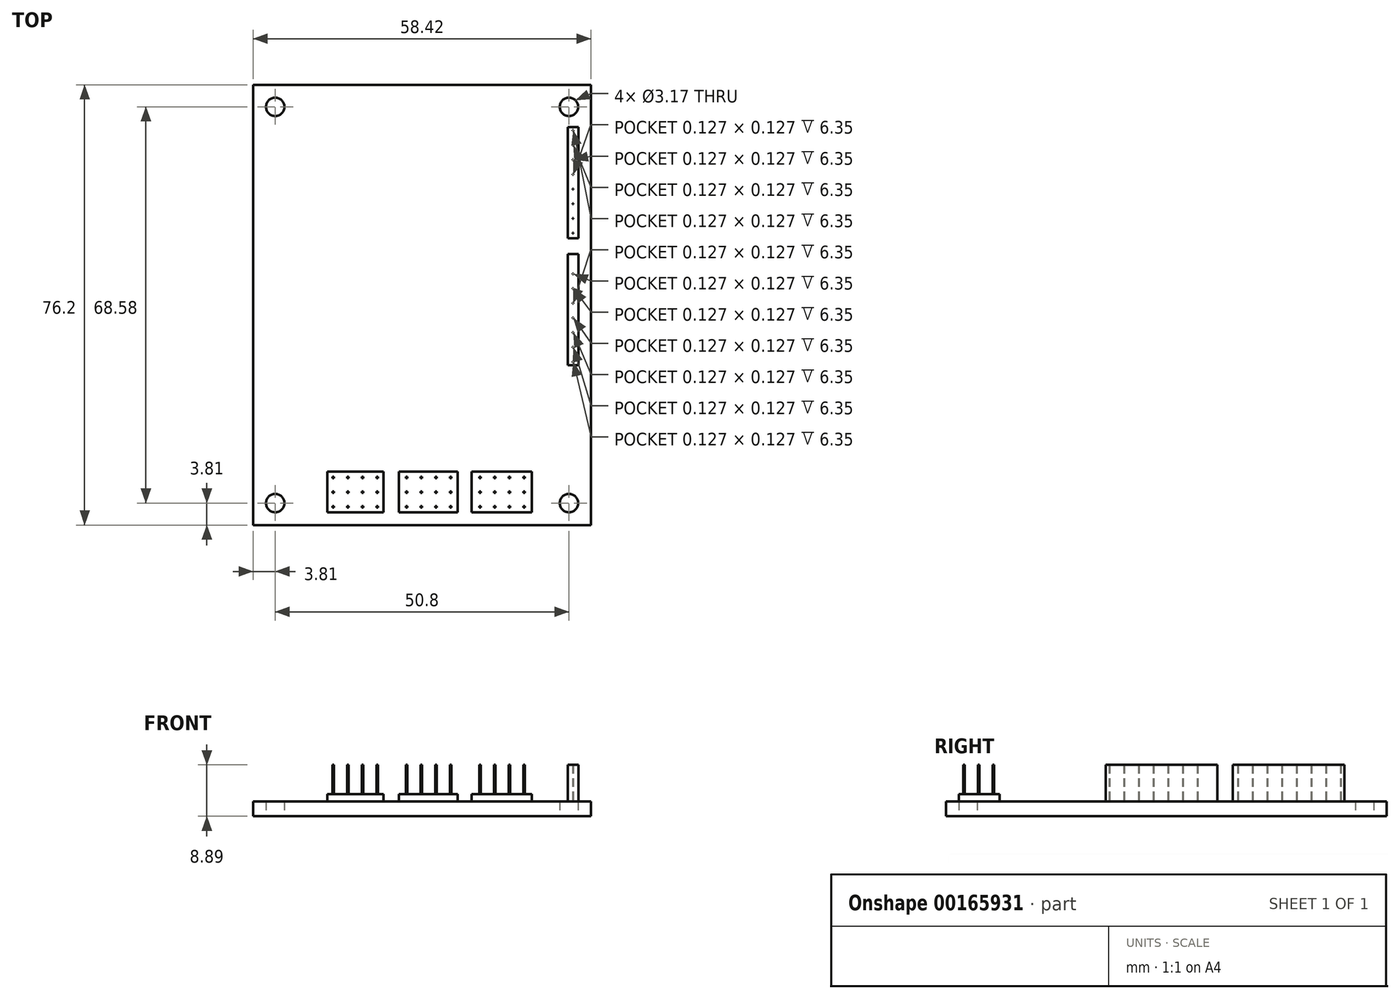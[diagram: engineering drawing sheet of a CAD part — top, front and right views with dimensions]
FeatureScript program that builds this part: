
annotation { "Feature Type Name" : "Feature", "Feature Type Description" : "" }
export const myFeature = defineFeature(function(context is Context, id is Id, definition is map)
    precondition{}
    {
        {
            var Q0;
            Q0=qCreatedBy(makeId("Top.planeOp"),FACE);
            var sketch = newSketch(context, id + "F0", { "sketchPlane" : qUnion([Q0])});
            skLineSegment(sketch, "E0.bottom", {"start": v(-29.21, 38.1) * mm, "end": v(29.21, 38.1) * mm});
            skLineSegment(sketch, "E0.top", {"start": v(-29.21, -38.1) * mm, "end": v(29.21, -38.1) * mm});
            skLineSegment(sketch, "E0.left", {"start": v(-29.21, 38.1) * mm, "end": v(-29.21, -38.1) * mm});
            skLineSegment(sketch, "E0.right", {"start": v(29.21, 38.1) * mm, "end": v(29.2, -38.1) * mm});
            skPoint(sketch, "E1", {"position": v(0, 38.1) * mm});
            skPoint(sketch, "E2", {"position": v(29.21, 0) * mm});
            skCircle(sketch, "E3", {"center": v(-25.4, 34.29) * mm, "radius": 1.59 * mm});
            skLineSegment(sketch, "E4", {"start": v(-25.4, 34.29) * mm, "end": v(-29.2, 34.29) * mm, "construction": true});
            skCircle(sketch, "E5.MirrorC", {"center": v(25.4, 34.29) * mm, "radius": 1.59 * mm});
            skCircle(sketch, "E6.MirrorC", {"center": v(-25.4, -34.29) * mm, "radius": 1.59 * mm});
            skCircle(sketch, "E7.MirrorC", {"center": v(25.4, -34.29) * mm, "radius": 1.59 * mm});
            skSolve(sketch);
        }
        {
            var Q0;
            Q0 = qSketchRegion(id + "F0", true);
            extrude(context, id + "F1", {"entities" : qUnion([Q0]), "depth" : 2.54 * mm});
        }
        {
            var Q0;
            Q0=makeQuery(id+"F1.opExtrude","CAP_FACE",FACE,{"disambiguationData":[OSD([sQuery(id+"F0.wireOp",EDGE,"E0.bottom"),sQuery(id+"F0.wireOp",EDGE,"E0.top"),sQuery(id+"F0.wireOp",EDGE,"E0.left"),sQuery(id+"F0.wireOp",EDGE,"E0.right"),sQuery(id+"F0.wireOp",EDGE,"E3"),sQuery(id+"F0.wireOp",EDGE,"E5.MirrorC"),sQuery(id+"F0.wireOp",EDGE,"E6.MirrorC"),sQuery(id+"F0.wireOp",EDGE,"E7.MirrorC")])],"isStart":false});
            var sketch = newSketch(context, id + "F2", { "sketchPlane" : qUnion([Q0])});
            skLineSegment(sketch, "E8.bottom", {"start": v(26.06, 12.48) * mm, "end": v(26.19, 12.48) * mm});
            skLineSegment(sketch, "E8.top", {"start": v(26.06, 12.35) * mm, "end": v(26.19, 12.35) * mm});
            skLineSegment(sketch, "E8.left", {"start": v(26.06, 12.48) * mm, "end": v(26.06, 12.35) * mm});
            skLineSegment(sketch, "E8.right", {"start": v(26.19, 12.48) * mm, "end": v(26.19, 12.35) * mm});
            skLineSegment(sketch, "E9.1.0.0", {"start": v(26.06, 14.89) * mm, "end": v(26.19, 14.89) * mm});
            skLineSegment(sketch, "E9.1.0.1", {"start": v(26.19, 15.02) * mm, "end": v(26.19, 14.89) * mm});
            skLineSegment(sketch, "E9.1.0.2", {"start": v(26.06, 15.02) * mm, "end": v(26.19, 15.02) * mm});
            skLineSegment(sketch, "E9.1.0.3", {"start": v(26.06, 15.02) * mm, "end": v(26.06, 14.89) * mm});
            skLineSegment(sketch, "E9.2.0.0", {"start": v(26.06, 17.43) * mm, "end": v(26.19, 17.43) * mm});
            skLineSegment(sketch, "E9.2.0.1", {"start": v(26.19, 17.56) * mm, "end": v(26.19, 17.43) * mm});
            skLineSegment(sketch, "E9.2.0.2", {"start": v(26.06, 17.56) * mm, "end": v(26.19, 17.56) * mm});
            skLineSegment(sketch, "E9.2.0.3", {"start": v(26.06, 17.56) * mm, "end": v(26.06, 17.43) * mm});
            skLineSegment(sketch, "E9.direction1", {"start": v(26.06, 12.35) * mm, "end": v(26.06, 14.89) * mm, "construction": true});
            skLineSegment(sketch, "E10.0.3.0", {"start": v(26.06, 19.97) * mm, "end": v(26.19, 19.97) * mm});
            skLineSegment(sketch, "E10.3.3.0", {"start": v(26.19, 20.1) * mm, "end": v(26.19, 19.97) * mm});
            skLineSegment(sketch, "E10.6.3.0", {"start": v(26.06, 20.1) * mm, "end": v(26.19, 20.1) * mm});
            skLineSegment(sketch, "E10.9.3.0", {"start": v(26.06, 20.1) * mm, "end": v(26.06, 19.97) * mm});
            skLineSegment(sketch, "E10.0.4.0", {"start": v(26.06, 22.5) * mm, "end": v(26.19, 22.5) * mm});
            skLineSegment(sketch, "E10.3.4.0", {"start": v(26.19, 22.64) * mm, "end": v(26.19, 22.5) * mm});
            skLineSegment(sketch, "E10.6.4.0", {"start": v(26.06, 22.64) * mm, "end": v(26.19, 22.64) * mm});
            skLineSegment(sketch, "E10.9.4.0", {"start": v(26.06, 22.64) * mm, "end": v(26.06, 22.5) * mm});
            skLineSegment(sketch, "E10.0.5.0", {"start": v(26.06, 25.05) * mm, "end": v(26.19, 25.05) * mm});
            skLineSegment(sketch, "E10.3.5.0", {"start": v(26.19, 25.18) * mm, "end": v(26.19, 25.05) * mm});
            skLineSegment(sketch, "E10.6.5.0", {"start": v(26.06, 25.18) * mm, "end": v(26.19, 25.18) * mm});
            skLineSegment(sketch, "E10.9.5.0", {"start": v(26.06, 25.18) * mm, "end": v(26.06, 25.05) * mm});
            skLineSegment(sketch, "E10.0.6.0", {"start": v(26.06, 27.59) * mm, "end": v(26.19, 27.59) * mm});
            skLineSegment(sketch, "E10.3.6.0", {"start": v(26.19, 27.72) * mm, "end": v(26.19, 27.59) * mm});
            skLineSegment(sketch, "E10.6.6.0", {"start": v(26.06, 27.72) * mm, "end": v(26.19, 27.72) * mm});
            skLineSegment(sketch, "E10.9.6.0", {"start": v(26.06, 27.72) * mm, "end": v(26.06, 27.59) * mm});
            skLineSegment(sketch, "E10.0.7.0", {"start": v(26.06, 30.13) * mm, "end": v(26.19, 30.13) * mm});
            skLineSegment(sketch, "E10.3.7.0", {"start": v(26.19, 30.26) * mm, "end": v(26.19, 30.13) * mm});
            skLineSegment(sketch, "E10.6.7.0", {"start": v(26.06, 30.26) * mm, "end": v(26.19, 30.26) * mm});
            skLineSegment(sketch, "E10.9.7.0", {"start": v(26.06, 30.26) * mm, "end": v(26.06, 30.13) * mm});
            skLineSegment(sketch, "E11.bottom", {"start": v(25.22, 30.8) * mm, "end": v(27.07, 30.8) * mm});
            skLineSegment(sketch, "E11.top", {"start": v(25.22, 11.52) * mm, "end": v(27.07, 11.52) * mm});
            skLineSegment(sketch, "E11.left", {"start": v(25.22, 30.8) * mm, "end": v(25.22, 11.52) * mm});
            skLineSegment(sketch, "E11.right", {"start": v(27.07, 30.8) * mm, "end": v(27.07, 11.52) * mm});
            skLineSegment(sketch, "E12", {"start": v(29.21, 10.17) * mm, "end": v(23.82, 10.17) * mm, "construction": true});
            skLineSegment(sketch, "E13.MirrorCS", {"start": v(25.22, -10.45) * mm, "end": v(25.22, 8.82) * mm});
            skLineSegment(sketch, "E14.MirrorCS", {"start": v(26.06, 8) * mm, "end": v(26.19, 8) * mm});
            skLineSegment(sketch, "E15.MirrorCS", {"start": v(26.06, 8) * mm, "end": v(26.06, 5.46) * mm, "construction": true});
            skLineSegment(sketch, "E16.MirrorCS", {"start": v(26.06, 7.87) * mm, "end": v(26.19, 7.87) * mm});
            skLineSegment(sketch, "E17.MirrorCS", {"start": v(26.19, 7.87) * mm, "end": v(26.19, 8) * mm});
            skLineSegment(sketch, "E18.MirrorCS", {"start": v(26.19, 5.33) * mm, "end": v(26.19, 5.46) * mm});
            skLineSegment(sketch, "E19.MirrorCS", {"start": v(26.06, 5.33) * mm, "end": v(26.19, 5.33) * mm});
            skLineSegment(sketch, "E20.MirrorCS", {"start": v(26.06, 5.33) * mm, "end": v(26.06, 5.46) * mm});
            skLineSegment(sketch, "E21.MirrorCS", {"start": v(26.06, 5.46) * mm, "end": v(26.19, 5.46) * mm});
            skLineSegment(sketch, "E22.MirrorCS", {"start": v(26.19, 2.79) * mm, "end": v(26.19, 2.92) * mm});
            skLineSegment(sketch, "E23.MirrorCS", {"start": v(26.06, 2.79) * mm, "end": v(26.19, 2.79) * mm});
            skLineSegment(sketch, "E24.MirrorCS", {"start": v(26.06, 2.79) * mm, "end": v(26.06, 2.92) * mm});
            skLineSegment(sketch, "E25.MirrorCS", {"start": v(26.06, 2.92) * mm, "end": v(26.19, 2.92) * mm});
            skLineSegment(sketch, "E26.MirrorCS", {"start": v(26.06, 0.38) * mm, "end": v(26.19, 0.38) * mm});
            skLineSegment(sketch, "E27.MirrorCS", {"start": v(26.19, 0.25) * mm, "end": v(26.19, 0.38) * mm});
            skLineSegment(sketch, "E28.MirrorCS", {"start": v(26.06, 0.25) * mm, "end": v(26.19, 0.25) * mm});
            skLineSegment(sketch, "E29.MirrorCS", {"start": v(26.06, 0.25) * mm, "end": v(26.06, 0.38) * mm});
            skLineSegment(sketch, "E30.MirrorCS", {"start": v(26.19, -2.3) * mm, "end": v(26.19, -2.16) * mm});
            skLineSegment(sketch, "E31.MirrorCS", {"start": v(26.06, -2.3) * mm, "end": v(26.19, -2.3) * mm});
            skLineSegment(sketch, "E32.MirrorCS", {"start": v(26.06, -2.3) * mm, "end": v(26.06, -2.16) * mm});
            skLineSegment(sketch, "E33.MirrorCS", {"start": v(26.06, -2.16) * mm, "end": v(26.19, -2.16) * mm});
            skLineSegment(sketch, "E34.MirrorCS", {"start": v(26.06, -7.37) * mm, "end": v(26.19, -7.37) * mm});
            skLineSegment(sketch, "E35.MirrorCS", {"start": v(26.06, -4.83) * mm, "end": v(26.19, -4.83) * mm});
            skLineSegment(sketch, "E36.MirrorCS", {"start": v(26.19, -7.37) * mm, "end": v(26.19, -7.24) * mm});
            skLineSegment(sketch, "E37.MirrorCS", {"start": v(26.19, -4.83) * mm, "end": v(26.19, -4.7) * mm});
            skLineSegment(sketch, "E38.MirrorCS", {"start": v(26.06, -4.83) * mm, "end": v(26.06, -4.7) * mm});
            skLineSegment(sketch, "E39.MirrorCS", {"start": v(26.06, -7.24) * mm, "end": v(26.19, -7.24) * mm});
            skLineSegment(sketch, "E40.MirrorCS", {"start": v(26.06, -4.7) * mm, "end": v(26.19, -4.7) * mm});
            skLineSegment(sketch, "E41.MirrorCS", {"start": v(26.06, -7.37) * mm, "end": v(26.06, -7.24) * mm});
            skLineSegment(sketch, "E42.MirrorCS", {"start": v(26.06, -9.78) * mm, "end": v(26.19, -9.78) * mm});
            skLineSegment(sketch, "E43.MirrorCS", {"start": v(26.06, -9.91) * mm, "end": v(26.19, -9.91) * mm});
            skLineSegment(sketch, "E44.MirrorCS", {"start": v(26.06, -9.91) * mm, "end": v(26.06, -9.78) * mm});
            skLineSegment(sketch, "E45.MirrorCS", {"start": v(26.19, -9.91) * mm, "end": v(26.19, -9.78) * mm});
            skLineSegment(sketch, "E46.MirrorCS", {"start": v(25.22, 8.82) * mm, "end": v(27.07, 8.82) * mm});
            skLineSegment(sketch, "E47.MirrorCS", {"start": v(27.07, -10.45) * mm, "end": v(27.07, 8.82) * mm});
            skLineSegment(sketch, "E48.MirrorCS", {"start": v(25.22, -10.45) * mm, "end": v(27.07, -10.45) * mm});
            skSolve(sketch);
        }
        {
            var Q0;
            Q0 = qSketchRegion(id + "F2", true);
            extrude(context, id + "F3", {"entities" : qUnion([Q0]), "operationType" : NewBodyOperationType.ADD, "depth" : 6.35 * mm});
        }
        {
            var Q0;
            {var subQ0=sQuery(id+"F0.wireOp",EDGE,"E0.left");var subQ1=sQuery(id+"F0.wireOp",EDGE,"E7.MirrorC");var subQ2=sQuery(id+"F0.wireOp",EDGE,"E6.MirrorC");var subQ3=sQuery(id+"F0.wireOp",EDGE,"E5.MirrorC");var subQ4=sQuery(id+"F0.wireOp",EDGE,"E3");var subQ5=sQuery(id+"F0.wireOp",EDGE,"E0.right");var subQ6=sQuery(id+"F0.wireOp",EDGE,"E0.bottom");var subQ7=sQuery(id+"F0.wireOp",EDGE,"E0.top");Q0=makeQuery(id+"F3.boolean.opBoolean","SPLIT",FACE,{"disambiguationData":[TD([makeQuery(id+"F1.opExtrude","SWEPT_FACE",FACE,{"disambiguationData":[OSD([subQ6])]})])],"derivedFrom":makeQuery(id+"F1.opExtrude","CAP_FACE",FACE,{"disambiguationData":[OSD([subQ6,subQ7,subQ0,subQ5,subQ4,subQ3,subQ2,subQ1])],"isStart":false})});}
            var sketch = newSketch(context, id + "F4", { "sketchPlane" : qUnion([Q0])});
            skLineSegment(sketch, "E49.bottom", {"start": v(-15.5, -34.83) * mm, "end": v(-15.24, -34.83) * mm});
            skLineSegment(sketch, "E49.top", {"start": v(-15.5, -35.09) * mm, "end": v(-15.24, -35.09) * mm});
            skLineSegment(sketch, "E49.left", {"start": v(-15.5, -34.83) * mm, "end": v(-15.5, -35.09) * mm});
            skLineSegment(sketch, "E49.right", {"start": v(-15.24, -34.83) * mm, "end": v(-15.24, -35.09) * mm});
            skLineSegment(sketch, "E50.1.0.0", {"start": v(-12.7, -34.83) * mm, "end": v(-12.7, -35.09) * mm});
            skLineSegment(sketch, "E50.1.0.1", {"start": v(-12.95, -34.83) * mm, "end": v(-12.95, -35.09) * mm});
            skLineSegment(sketch, "E50.1.0.2", {"start": v(-12.95, -34.83) * mm, "end": v(-12.7, -34.83) * mm});
            skLineSegment(sketch, "E50.1.0.3", {"start": v(-12.95, -35.09) * mm, "end": v(-12.7, -35.09) * mm});
            skLineSegment(sketch, "E50.2.0.0", {"start": v(-10.16, -34.83) * mm, "end": v(-10.16, -35.09) * mm});
            skLineSegment(sketch, "E50.2.0.1", {"start": v(-10.41, -34.83) * mm, "end": v(-10.41, -35.09) * mm});
            skLineSegment(sketch, "E50.2.0.2", {"start": v(-10.41, -34.83) * mm, "end": v(-10.16, -34.83) * mm});
            skLineSegment(sketch, "E50.2.0.3", {"start": v(-10.41, -35.09) * mm, "end": v(-10.16, -35.09) * mm});
            skLineSegment(sketch, "E50.3.0.0", {"start": v(-7.62, -34.83) * mm, "end": v(-7.62, -35.09) * mm});
            skLineSegment(sketch, "E50.3.0.1", {"start": v(-7.87, -34.83) * mm, "end": v(-7.87, -35.09) * mm});
            skLineSegment(sketch, "E50.3.0.2", {"start": v(-7.87, -34.83) * mm, "end": v(-7.62, -34.83) * mm});
            skLineSegment(sketch, "E50.3.0.3", {"start": v(-7.87, -35.09) * mm, "end": v(-7.62, -35.09) * mm});
            skLineSegment(sketch, "E50.direction1", {"start": v(-15.5, -35.09) * mm, "end": v(-12.95, -35.09) * mm, "construction": true});
            skLineSegment(sketch, "E51.1.0.0", {"start": v(-15.5, -32.55) * mm, "end": v(-12.95, -32.55) * mm, "construction": true});
            skLineSegment(sketch, "E51.1.0.1", {"start": v(-7.87, -32.3) * mm, "end": v(-7.62, -32.3) * mm});
            skLineSegment(sketch, "E51.1.0.2", {"start": v(-7.87, -32.3) * mm, "end": v(-7.87, -32.55) * mm});
            skLineSegment(sketch, "E51.1.0.3", {"start": v(-7.87, -32.55) * mm, "end": v(-7.62, -32.55) * mm});
            skLineSegment(sketch, "E51.1.0.4", {"start": v(-15.5, -32.3) * mm, "end": v(-15.24, -32.3) * mm});
            skLineSegment(sketch, "E51.1.0.5", {"start": v(-15.5, -32.3) * mm, "end": v(-15.5, -32.55) * mm});
            skLineSegment(sketch, "E51.1.0.6", {"start": v(-15.24, -32.3) * mm, "end": v(-15.24, -32.55) * mm});
            skLineSegment(sketch, "E51.1.0.7", {"start": v(-12.7, -32.3) * mm, "end": v(-12.7, -32.55) * mm});
            skLineSegment(sketch, "E51.1.0.8", {"start": v(-12.95, -32.3) * mm, "end": v(-12.7, -32.3) * mm});
            skLineSegment(sketch, "E51.1.0.9", {"start": v(-10.16, -32.3) * mm, "end": v(-10.16, -32.55) * mm});
            skLineSegment(sketch, "E51.1.0.10", {"start": v(-10.41, -32.3) * mm, "end": v(-10.41, -32.55) * mm});
            skLineSegment(sketch, "E51.1.0.11", {"start": v(-10.41, -32.3) * mm, "end": v(-10.16, -32.3) * mm});
            skLineSegment(sketch, "E51.1.0.12", {"start": v(-10.41, -32.55) * mm, "end": v(-10.16, -32.55) * mm});
            skLineSegment(sketch, "E51.1.0.13", {"start": v(-7.62, -32.3) * mm, "end": v(-7.62, -32.55) * mm});
            skLineSegment(sketch, "E51.1.0.14", {"start": v(-15.5, -32.55) * mm, "end": v(-15.24, -32.55) * mm});
            skLineSegment(sketch, "E51.1.0.15", {"start": v(-12.95, -32.3) * mm, "end": v(-12.95, -32.55) * mm});
            skLineSegment(sketch, "E51.1.0.16", {"start": v(-12.95, -32.55) * mm, "end": v(-12.7, -32.55) * mm});
            skLineSegment(sketch, "E51.2.0.0", {"start": v(-15.5, -30) * mm, "end": v(-12.95, -30) * mm, "construction": true});
            skLineSegment(sketch, "E51.2.0.1", {"start": v(-7.87, -29.75) * mm, "end": v(-7.62, -29.75) * mm});
            skLineSegment(sketch, "E51.2.0.2", {"start": v(-7.87, -29.75) * mm, "end": v(-7.87, -30) * mm});
            skLineSegment(sketch, "E51.2.0.3", {"start": v(-7.87, -30) * mm, "end": v(-7.62, -30) * mm});
            skLineSegment(sketch, "E51.2.0.4", {"start": v(-15.5, -29.75) * mm, "end": v(-15.24, -29.75) * mm});
            skLineSegment(sketch, "E51.2.0.5", {"start": v(-15.5, -29.75) * mm, "end": v(-15.5, -30) * mm});
            skLineSegment(sketch, "E51.2.0.6", {"start": v(-15.24, -29.75) * mm, "end": v(-15.24, -30) * mm});
            skLineSegment(sketch, "E51.2.0.7", {"start": v(-12.7, -29.75) * mm, "end": v(-12.7, -30) * mm});
            skLineSegment(sketch, "E51.2.0.8", {"start": v(-12.95, -29.75) * mm, "end": v(-12.7, -29.75) * mm});
            skLineSegment(sketch, "E51.2.0.9", {"start": v(-10.16, -29.75) * mm, "end": v(-10.16, -30) * mm});
            skLineSegment(sketch, "E51.2.0.10", {"start": v(-10.41, -29.75) * mm, "end": v(-10.41, -30) * mm});
            skLineSegment(sketch, "E51.2.0.11", {"start": v(-10.41, -29.75) * mm, "end": v(-10.16, -29.75) * mm});
            skLineSegment(sketch, "E51.2.0.12", {"start": v(-10.41, -30) * mm, "end": v(-10.16, -30) * mm});
            skLineSegment(sketch, "E51.2.0.13", {"start": v(-7.62, -29.75) * mm, "end": v(-7.62, -30) * mm});
            skLineSegment(sketch, "E51.2.0.14", {"start": v(-15.5, -30) * mm, "end": v(-15.24, -30) * mm});
            skLineSegment(sketch, "E51.2.0.15", {"start": v(-12.95, -29.75) * mm, "end": v(-12.95, -30) * mm});
            skLineSegment(sketch, "E51.2.0.16", {"start": v(-12.95, -30) * mm, "end": v(-12.7, -30) * mm});
            skLineSegment(sketch, "E51.direction1", {"start": v(-15.5, -35.09) * mm, "end": v(-15.5, -32.55) * mm, "construction": true});
            skLineSegment(sketch, "E52.1.0.0", {"start": v(-2.8, -35.09) * mm, "end": v(-2.8, -32.55) * mm, "construction": true});
            skLineSegment(sketch, "E52.1.0.1", {"start": v(-2.8, -30) * mm, "end": v(-0.25, -30) * mm, "construction": true});
            skLineSegment(sketch, "E52.1.0.2", {"start": v(-2.8, -35.09) * mm, "end": v(-0.25, -35.09) * mm, "construction": true});
            skLineSegment(sketch, "E52.1.0.3", {"start": v(-2.8, -32.55) * mm, "end": v(-0.25, -32.55) * mm, "construction": true});
            skLineSegment(sketch, "E52.1.0.4", {"start": v(2.29, -32.3) * mm, "end": v(2.29, -32.55) * mm});
            skLineSegment(sketch, "E52.1.0.5", {"start": v(4.83, -32.3) * mm, "end": v(4.83, -32.55) * mm});
            skLineSegment(sketch, "E52.1.0.6", {"start": v(4.83, -29.75) * mm, "end": v(5.08, -29.75) * mm});
            skLineSegment(sketch, "E52.1.0.7", {"start": v(4.83, -32.3) * mm, "end": v(5.08, -32.3) * mm});
            skLineSegment(sketch, "E52.1.0.8", {"start": v(2.29, -32.55) * mm, "end": v(2.54, -32.55) * mm});
            skLineSegment(sketch, "E52.1.0.9", {"start": v(4.83, -29.75) * mm, "end": v(4.83, -30) * mm});
            skLineSegment(sketch, "E52.1.0.10", {"start": v(4.83, -32.55) * mm, "end": v(5.08, -32.55) * mm});
            skLineSegment(sketch, "E52.1.0.11", {"start": v(2.29, -29.75) * mm, "end": v(2.54, -29.75) * mm});
            skLineSegment(sketch, "E52.1.0.12", {"start": v(4.83, -34.83) * mm, "end": v(5.08, -34.83) * mm});
            skLineSegment(sketch, "E52.1.0.13", {"start": v(4.83, -35.09) * mm, "end": v(5.08, -35.09) * mm});
            skLineSegment(sketch, "E52.1.0.14", {"start": v(2.29, -34.83) * mm, "end": v(2.29, -35.09) * mm});
            skLineSegment(sketch, "E52.1.0.15", {"start": v(2.29, -34.83) * mm, "end": v(2.54, -34.83) * mm});
            skLineSegment(sketch, "E52.1.0.16", {"start": v(2.29, -29.75) * mm, "end": v(2.29, -30) * mm});
            skLineSegment(sketch, "E52.1.0.17", {"start": v(2.29, -32.3) * mm, "end": v(2.54, -32.3) * mm});
            skLineSegment(sketch, "E52.1.0.18", {"start": v(2.29, -35.09) * mm, "end": v(2.54, -35.09) * mm});
            skLineSegment(sketch, "E52.1.0.19", {"start": v(5.08, -34.83) * mm, "end": v(5.08, -35.09) * mm});
            skLineSegment(sketch, "E52.1.0.20", {"start": v(4.83, -30) * mm, "end": v(5.08, -30) * mm});
            skLineSegment(sketch, "E52.1.0.21", {"start": v(5.08, -32.3) * mm, "end": v(5.08, -32.55) * mm});
            skLineSegment(sketch, "E52.1.0.22", {"start": v(2.29, -30) * mm, "end": v(2.54, -30) * mm});
            skLineSegment(sketch, "E52.1.0.23", {"start": v(-2.8, -30) * mm, "end": v(-2.54, -30) * mm});
            skLineSegment(sketch, "E52.1.0.24", {"start": v(2.54, -29.75) * mm, "end": v(2.54, -30) * mm});
            skLineSegment(sketch, "E52.1.0.25", {"start": v(2.54, -32.3) * mm, "end": v(2.54, -32.55) * mm});
            skLineSegment(sketch, "E52.1.0.26", {"start": v(-0.25, -29.75) * mm, "end": v(0, -29.75) * mm});
            skLineSegment(sketch, "E52.1.0.27", {"start": v(-0.25, -30) * mm, "end": v(0, -30) * mm});
            skLineSegment(sketch, "E52.1.0.28", {"start": v(5.08, -29.75) * mm, "end": v(5.08, -30) * mm});
            skLineSegment(sketch, "E52.1.0.29", {"start": v(-2.8, -29.75) * mm, "end": v(-2.54, -29.75) * mm});
            skLineSegment(sketch, "E52.1.0.30", {"start": v(0, -29.75) * mm, "end": v(0, -30) * mm});
            skLineSegment(sketch, "E52.1.0.31", {"start": v(4.83, -34.83) * mm, "end": v(4.83, -35.09) * mm});
            skLineSegment(sketch, "E52.1.0.32", {"start": v(-2.8, -29.75) * mm, "end": v(-2.8, -30) * mm});
            skLineSegment(sketch, "E52.1.0.33", {"start": v(-0.25, -29.75) * mm, "end": v(-0.25, -30) * mm});
            skLineSegment(sketch, "E52.1.0.34", {"start": v(2.54, -34.83) * mm, "end": v(2.54, -35.09) * mm});
            skLineSegment(sketch, "E52.1.0.35", {"start": v(-2.54, -29.75) * mm, "end": v(-2.54, -30) * mm});
            skLineSegment(sketch, "E52.1.0.36", {"start": v(-0.25, -32.3) * mm, "end": v(-0.25, -32.55) * mm});
            skLineSegment(sketch, "E52.1.0.37", {"start": v(-0.25, -32.3) * mm, "end": v(0, -32.3) * mm});
            skLineSegment(sketch, "E52.1.0.38", {"start": v(-2.8, -34.83) * mm, "end": v(-2.54, -34.83) * mm});
            skLineSegment(sketch, "E52.1.0.39", {"start": v(-2.8, -35.09) * mm, "end": v(-2.54, -35.09) * mm});
            skLineSegment(sketch, "E52.1.0.40", {"start": v(-2.8, -34.83) * mm, "end": v(-2.8, -35.09) * mm});
            skLineSegment(sketch, "E52.1.0.41", {"start": v(-2.54, -34.83) * mm, "end": v(-2.54, -35.09) * mm});
            skLineSegment(sketch, "E52.1.0.42", {"start": v(0, -34.83) * mm, "end": v(0, -35.09) * mm});
            skLineSegment(sketch, "E52.1.0.43", {"start": v(-0.25, -34.83) * mm, "end": v(0, -34.83) * mm});
            skLineSegment(sketch, "E52.1.0.44", {"start": v(-0.25, -35.09) * mm, "end": v(0, -35.09) * mm});
            skLineSegment(sketch, "E52.1.0.45", {"start": v(0, -32.3) * mm, "end": v(0, -32.55) * mm});
            skLineSegment(sketch, "E52.1.0.46", {"start": v(-0.25, -32.55) * mm, "end": v(0, -32.55) * mm});
            skLineSegment(sketch, "E52.1.0.47", {"start": v(-2.8, -32.3) * mm, "end": v(-2.8, -32.55) * mm});
            skLineSegment(sketch, "E52.1.0.48", {"start": v(-2.8, -32.55) * mm, "end": v(-2.54, -32.55) * mm});
            skLineSegment(sketch, "E52.1.0.49", {"start": v(-2.54, -32.3) * mm, "end": v(-2.54, -32.55) * mm});
            skLineSegment(sketch, "E52.1.0.50", {"start": v(-0.25, -34.83) * mm, "end": v(-0.25, -35.09) * mm});
            skLineSegment(sketch, "E52.1.0.51", {"start": v(-2.8, -32.3) * mm, "end": v(-2.54, -32.3) * mm});
            skLineSegment(sketch, "E52.2.0.0", {"start": v(9.9, -35.09) * mm, "end": v(9.9, -32.55) * mm, "construction": true});
            skLineSegment(sketch, "E52.2.0.1", {"start": v(9.9, -30) * mm, "end": v(12.45, -30) * mm, "construction": true});
            skLineSegment(sketch, "E52.2.0.2", {"start": v(9.9, -35.09) * mm, "end": v(12.45, -35.09) * mm, "construction": true});
            skLineSegment(sketch, "E52.2.0.3", {"start": v(9.9, -32.55) * mm, "end": v(12.45, -32.55) * mm, "construction": true});
            skLineSegment(sketch, "E52.2.0.4", {"start": v(14.99, -32.3) * mm, "end": v(14.99, -32.55) * mm});
            skLineSegment(sketch, "E52.2.0.5", {"start": v(17.53, -32.3) * mm, "end": v(17.53, -32.55) * mm});
            skLineSegment(sketch, "E52.2.0.6", {"start": v(17.53, -29.75) * mm, "end": v(17.78, -29.75) * mm});
            skLineSegment(sketch, "E52.2.0.7", {"start": v(17.53, -32.3) * mm, "end": v(17.78, -32.3) * mm});
            skLineSegment(sketch, "E52.2.0.8", {"start": v(14.99, -32.55) * mm, "end": v(15.24, -32.55) * mm});
            skLineSegment(sketch, "E52.2.0.9", {"start": v(17.53, -29.75) * mm, "end": v(17.53, -30) * mm});
            skLineSegment(sketch, "E52.2.0.10", {"start": v(17.53, -32.55) * mm, "end": v(17.78, -32.55) * mm});
            skLineSegment(sketch, "E52.2.0.11", {"start": v(14.99, -29.75) * mm, "end": v(15.24, -29.75) * mm});
            skLineSegment(sketch, "E52.2.0.12", {"start": v(17.53, -34.83) * mm, "end": v(17.78, -34.83) * mm});
            skLineSegment(sketch, "E52.2.0.13", {"start": v(17.53, -35.09) * mm, "end": v(17.78, -35.09) * mm});
            skLineSegment(sketch, "E52.2.0.14", {"start": v(14.99, -34.83) * mm, "end": v(14.99, -35.09) * mm});
            skLineSegment(sketch, "E52.2.0.15", {"start": v(14.99, -34.83) * mm, "end": v(15.24, -34.83) * mm});
            skLineSegment(sketch, "E52.2.0.16", {"start": v(14.99, -29.75) * mm, "end": v(14.99, -30) * mm});
            skLineSegment(sketch, "E52.2.0.17", {"start": v(14.99, -32.3) * mm, "end": v(15.24, -32.3) * mm});
            skLineSegment(sketch, "E52.2.0.18", {"start": v(14.99, -35.09) * mm, "end": v(15.24, -35.09) * mm});
            skLineSegment(sketch, "E52.2.0.19", {"start": v(17.78, -34.83) * mm, "end": v(17.78, -35.09) * mm});
            skLineSegment(sketch, "E52.2.0.20", {"start": v(17.53, -30) * mm, "end": v(17.78, -30) * mm});
            skLineSegment(sketch, "E52.2.0.21", {"start": v(17.78, -32.3) * mm, "end": v(17.78, -32.55) * mm});
            skLineSegment(sketch, "E52.2.0.22", {"start": v(14.99, -30) * mm, "end": v(15.24, -30) * mm});
            skLineSegment(sketch, "E52.2.0.23", {"start": v(9.9, -30) * mm, "end": v(10.16, -30) * mm});
            skLineSegment(sketch, "E52.2.0.24", {"start": v(15.24, -29.75) * mm, "end": v(15.24, -30) * mm});
            skLineSegment(sketch, "E52.2.0.25", {"start": v(15.24, -32.3) * mm, "end": v(15.24, -32.55) * mm});
            skLineSegment(sketch, "E52.2.0.26", {"start": v(12.45, -29.75) * mm, "end": v(12.7, -29.75) * mm});
            skLineSegment(sketch, "E52.2.0.27", {"start": v(12.45, -30) * mm, "end": v(12.7, -30) * mm});
            skLineSegment(sketch, "E52.2.0.28", {"start": v(17.78, -29.75) * mm, "end": v(17.78, -30) * mm});
            skLineSegment(sketch, "E52.2.0.29", {"start": v(9.9, -29.75) * mm, "end": v(10.16, -29.75) * mm});
            skLineSegment(sketch, "E52.2.0.30", {"start": v(12.7, -29.75) * mm, "end": v(12.7, -30) * mm});
            skLineSegment(sketch, "E52.2.0.31", {"start": v(17.53, -34.83) * mm, "end": v(17.53, -35.09) * mm});
            skLineSegment(sketch, "E52.2.0.32", {"start": v(9.9, -29.75) * mm, "end": v(9.9, -30) * mm});
            skLineSegment(sketch, "E52.2.0.33", {"start": v(12.45, -29.75) * mm, "end": v(12.45, -30) * mm});
            skLineSegment(sketch, "E52.2.0.34", {"start": v(15.24, -34.83) * mm, "end": v(15.24, -35.09) * mm});
            skLineSegment(sketch, "E52.2.0.35", {"start": v(10.16, -29.75) * mm, "end": v(10.16, -30) * mm});
            skLineSegment(sketch, "E52.2.0.36", {"start": v(12.45, -32.3) * mm, "end": v(12.45, -32.55) * mm});
            skLineSegment(sketch, "E52.2.0.37", {"start": v(12.45, -32.3) * mm, "end": v(12.7, -32.3) * mm});
            skLineSegment(sketch, "E52.2.0.38", {"start": v(9.9, -34.83) * mm, "end": v(10.16, -34.83) * mm});
            skLineSegment(sketch, "E52.2.0.39", {"start": v(9.9, -35.09) * mm, "end": v(10.16, -35.09) * mm});
            skLineSegment(sketch, "E52.2.0.40", {"start": v(9.9, -34.83) * mm, "end": v(9.9, -35.09) * mm});
            skLineSegment(sketch, "E52.2.0.41", {"start": v(10.16, -34.83) * mm, "end": v(10.16, -35.09) * mm});
            skLineSegment(sketch, "E52.2.0.42", {"start": v(12.7, -34.83) * mm, "end": v(12.7, -35.09) * mm});
            skLineSegment(sketch, "E52.2.0.43", {"start": v(12.45, -34.83) * mm, "end": v(12.7, -34.83) * mm});
            skLineSegment(sketch, "E52.2.0.44", {"start": v(12.45, -35.09) * mm, "end": v(12.7, -35.09) * mm});
            skLineSegment(sketch, "E52.2.0.45", {"start": v(12.7, -32.3) * mm, "end": v(12.7, -32.55) * mm});
            skLineSegment(sketch, "E52.2.0.46", {"start": v(12.45, -32.55) * mm, "end": v(12.7, -32.55) * mm});
            skLineSegment(sketch, "E52.2.0.47", {"start": v(9.9, -32.3) * mm, "end": v(9.9, -32.55) * mm});
            skLineSegment(sketch, "E52.2.0.48", {"start": v(9.9, -32.55) * mm, "end": v(10.16, -32.55) * mm});
            skLineSegment(sketch, "E52.2.0.49", {"start": v(10.16, -32.3) * mm, "end": v(10.16, -32.55) * mm});
            skLineSegment(sketch, "E52.2.0.50", {"start": v(12.45, -34.83) * mm, "end": v(12.45, -35.09) * mm});
            skLineSegment(sketch, "E52.2.0.51", {"start": v(9.9, -32.3) * mm, "end": v(10.16, -32.3) * mm});
            skLineSegment(sketch, "E52.direction1", {"start": v(-15.5, -35.09) * mm, "end": v(-2.8, -35.09) * mm, "construction": true});
            skSolve(sketch);
        }
        {
            var Q0;
            Q0 = qSketchRegion(id + "F4", true);
            extrude(context, id + "F5", {"entities" : qUnion([Q0]), "operationType" : NewBodyOperationType.ADD, "depth" : 6.35 * mm});
        }
        {
            var Q0;
            {var subQ0=sQuery(id+"F0.wireOp",EDGE,"E0.left");var subQ1=sQuery(id+"F0.wireOp",EDGE,"E7.MirrorC");var subQ2=sQuery(id+"F0.wireOp",EDGE,"E6.MirrorC");var subQ3=sQuery(id+"F0.wireOp",EDGE,"E5.MirrorC");var subQ4=sQuery(id+"F0.wireOp",EDGE,"E3");var subQ5=sQuery(id+"F0.wireOp",EDGE,"E0.right");var subQ6=sQuery(id+"F0.wireOp",EDGE,"E0.bottom");var subQ7=sQuery(id+"F0.wireOp",EDGE,"E0.top");Q0=makeQuery(id+"F3.boolean.opBoolean","SPLIT",FACE,{"disambiguationData":[TD([makeQuery(id+"F1.opExtrude","SWEPT_FACE",FACE,{"disambiguationData":[OSD([subQ6])]})])],"derivedFrom":makeQuery(id+"F1.opExtrude","CAP_FACE",FACE,{"disambiguationData":[OSD([subQ6,subQ7,subQ0,subQ5,subQ4,subQ3,subQ2,subQ1])],"isStart":false})});}
            var sketch = newSketch(context, id + "F6", { "sketchPlane" : qUnion([Q0])});
            skLineSegment(sketch, "E53.bottom", {"start": v(-16.4, -28.86) * mm, "end": v(-6.7, -28.86) * mm});
            skLineSegment(sketch, "E53.top", {"start": v(-16.4, -35.88) * mm, "end": v(-6.7, -35.88) * mm});
            skLineSegment(sketch, "E53.left", {"start": v(-16.4, -28.86) * mm, "end": v(-16.4, -35.88) * mm});
            skLineSegment(sketch, "E53.right", {"start": v(-6.7, -28.86) * mm, "end": v(-6.7, -35.88) * mm});
            skLineSegment(sketch, "E54.bottom", {"start": v(-4.02, -28.86) * mm, "end": v(6.13, -28.86) * mm});
            skLineSegment(sketch, "E54.top", {"start": v(-4.02, -35.88) * mm, "end": v(6.13, -35.88) * mm});
            skLineSegment(sketch, "E54.left", {"start": v(-4.02, -28.86) * mm, "end": v(-4.02, -35.88) * mm});
            skLineSegment(sketch, "E54.right", {"start": v(6.13, -28.86) * mm, "end": v(6.13, -35.88) * mm});
            skLineSegment(sketch, "E55.bottom", {"start": v(8.57, -28.86) * mm, "end": v(18.97, -28.86) * mm});
            skLineSegment(sketch, "E55.top", {"start": v(8.57, -35.88) * mm, "end": v(18.97, -35.88) * mm});
            skLineSegment(sketch, "E55.left", {"start": v(8.57, -28.86) * mm, "end": v(8.57, -35.88) * mm});
            skLineSegment(sketch, "E55.right", {"start": v(18.97, -28.86) * mm, "end": v(18.97, -35.88) * mm});
            skSolve(sketch);
        }
        {
            var Q0;
            Q0 = qSketchRegion(id + "F6", true);
            extrude(context, id + "F7", {"entities" : qUnion([Q0]), "operationType" : NewBodyOperationType.ADD, "depth" : 1.27 * mm});
        }
    });
